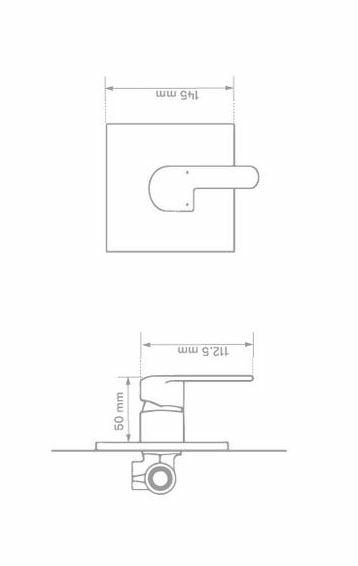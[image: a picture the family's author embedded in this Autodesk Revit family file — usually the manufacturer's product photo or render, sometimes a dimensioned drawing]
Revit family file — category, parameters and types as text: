
# Revit family: 01-1534-211 CONJUNTO REGISTRO DUCHA PIANA
name_source: partatom
category: Plumbing Fixtures
revit_build: Autodesk Revit 2018 (Build: 20170223_1515(x64)
units: mm (PartAtom-declared; Revit-internal decimal feet)

## family parameters
Cut with Voids When Loaded = No
Host = Face
OmniClass Number = 23.31.11.00
Part Type = Normal
Room Calculation Point = No
Round Connector Dimension = Use Diameter
Shared = No

## types (1)
- 01-1534-211
    Alto manija = 85 mm  [stored 0.278871 ft]
    Ancho manija = 75 mm
    CW Connection = Yes
    Default Elevation = 0 mm  [stored 0 ft]
    Description = Mezclador ducha
    Escudo = 56 mm  [stored 0.183727 ft]
    Ficha tecnica = No encontrada en internet
    HW Connection = Yes
    Laton = Laton
    Manufacturer = Gricol
    Metal Laton Cromado = Metal Laton Cromado
    Model = 01-1534-211
    Plastico - ABS Cromado = Plastico ABS Cromado
    Product Name = CONJUNTO REGISTRO DUCHA PIANA
    Sepacion entre registro y ducha = 400 mm  [stored 1.31234 ft]
    Type Image = <None>
    URL = https://www.gricol.com
    Vent Connection = No
    Waste Connection = No

note: [stored X ft] marks values corroborated as IEEE doubles in the binary element streams (Revit-internal decimal feet)

## geometry (parser evidence)
native form markers: Blend x4, Sweep x21
no freeform markers — native parametric forms only
